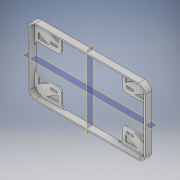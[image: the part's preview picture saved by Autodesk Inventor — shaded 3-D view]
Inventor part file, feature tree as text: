
AUTODESK INVENTOR PART (.ipt)
format: ipt  version: 2018 (Build 220112000, 112)  size: 340,992 bytes
history: native  units: in
note: dims shown in document units (in); Inventor stores cm internally (conversion verified against a paired STEP export)
features: reference x32, extrude x5, sketch x5, other x4, plane x2, projected_geometry x1
ambient origin geometry x8: Origin, YZ Plane, XZ Plane, XY Plane, X Axis, Y Axis, Z Axis, Center Point
bodies: Body1 (feature_tree)
feature tree (49):
  extrude  "Extrusion3"  Depth=0.15in
  extrude  "Extrusion4"  Depth=1.1in
  plane  "Work Plane1"
  plane  "Work Plane2"
  extrude  "Extrusion7"  Depth=0.25in
  extrude  "Extrusion8"  Depth=0.0827in
  extrude  "Extrusion9"  Depth=0.0827in
  sketch  "Sketch1"  dims[d1=0.9264in d2=0.15in]
  reference  "Reference1"
  reference  "Reference2"
  reference  "Reference3"
  reference  "Reference4"
  reference  "Reference6"
  reference  "Reference7"
  reference  "Reference8"
  reference  "Reference9"
  reference  "Reference10"
  reference  "Reference11"
  reference  "Reference12"
  reference  "Reference13"
  reference  "Reference17"
  reference  "Reference18"
  reference  "Reference19"
  reference  "Reference20"
  sketch  "Sketch4"  dims[d5=0.15in d16=1.1in]
  projected_geometry  "Projected Loop4"
  sketch  "Sketch9"  dims[d18=0.25in d21=0.25in]
  reference  "Reference23"
  reference  "Reference24"
  reference  "Reference25"
  reference  "Reference26"
  reference  "Reference27"
  reference  "Reference28"
  reference  "Reference29"
  reference  "Reference30"
  reference  "Reference31"
  reference  "Reference32"
  reference  "Reference33"
  reference  "Reference34"
  reference  "Reference35"
  reference  "Reference36"
  reference  "Reference37"
  reference  "Reference38"
  sketch  "Sketch10"  dims[d22=0.25in d23=0.0827in]
  sketch  "Sketch11"  dims[d24=0.0827in d25=0.0827in d33=0.2in d34=0.2in d35=0.2in d36=0.25in d37=0.25in d38=0.0827in d39=0.0in d40=0.0827in d41=0.3346in d42=0.0in d73=0.02in d74=0.02in d75=0.1in d76=0.1in d77=0.28in d78=0.1in d79=0.1in d80=0.02in d81=0.02in d82=0.28in d83=0.0866in d84=0.0in d85=0.7in d86=0.75in d87=0.4in d88=0.3in d89=0.3in d90=0.0866in d91=0.0in d92=0.15in d93=0.075in d94=0.075in d95=0.15in d96=0.33in d97=0.075in d98=0.075in d99=0.075in d100=0.15in d101=0.33in d102=1.1in d103=0.0in d104=0.0in]
  other  "<userpath>\Desktop\LocalGit\seniorproject\hardware\mechanical\Hub\Hub Assembly.iam"
  other  "Hub Assembly.iam"
  other  "Hub Enclosure Back:1"
  other  "Touchscreen:1"
